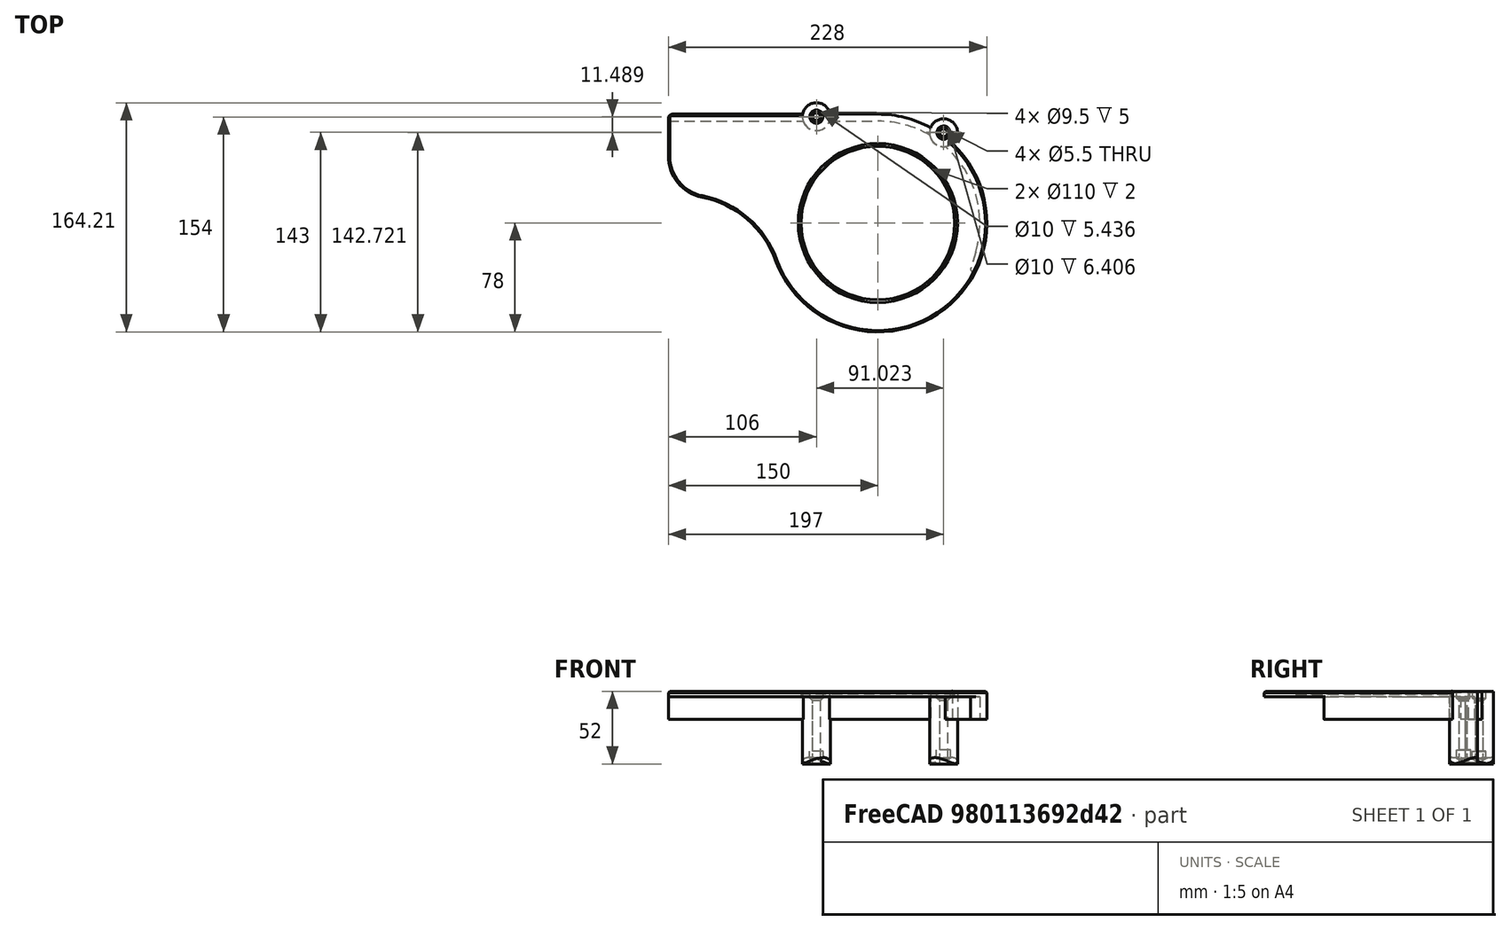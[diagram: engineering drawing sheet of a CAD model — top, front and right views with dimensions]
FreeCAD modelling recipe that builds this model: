
FCSTD DOCUMENT  (FreeCAD 0.19R)
Label: R2
License: All rights reserved
LicenseURL: http://en.wikipedia.org/wiki/All_rights_reserved
objects: Sketcher::SketchObject×5, Part::Cylinder×4, PartDesign::Pocket×3, PartDesign::Chamfer×3, PartDesign::Pad×2, PartDesign::Fillet×2, Part::MultiFuse×2, Part::Cut×2, PartDesign::Body×1, Mesh::Feature×1
note: 34 computed .brp shape members not serialized (recipe doc carries the construction recipe); baked Part::Feature solids carry a one-line shape summary decoded from their .brp

FEATURE [Sketcher::SketchObject] Sketch
  FullyConstrained = true
  MapMode = 5
  Support = -> [XY_Plane]
  sketch-geometry (10):
    g0: LineSegment StartX=0 StartY=0 StartZ=0 EndX=121.094 EndY=169.768 EndZ=0
    g1: LineSegment StartX=-81.2548 StartY=143.617 StartZ=0 EndX=0 EndY=0 EndZ=0
    g2: Circle CenterX=0 CenterY=0 CenterZ=0 NormalX=0 NormalY=0 NormalZ=1 AngleXU=0 Radius=73
    g3: LineSegment StartX=-228.06 StartY=73 StartZ=0 EndX=0 EndY=73 EndZ=0
    g4: LineSegment StartX=2.39e-14 StartY=78 StartZ=0 EndX=-150 EndY=78 EndZ=0
    g5: ArcOfCircle CenterX=0 CenterY=0 CenterZ=0 NormalX=0 NormalY=0 NormalZ=1 AngleXU=0 Radius=78 StartAngle=3.48916 EndAngle=7.85398
    g6: LineSegment StartX=-150 StartY=78 StartZ=0 EndX=-150 EndY=48 EndZ=0
    g7: ArcOfCircle CenterX=-120 CenterY=48 CenterZ=0 NormalX=0 NormalY=0 NormalZ=1 AngleXU=0 Radius=30 StartAngle=3.14159 EndAngle=4.51567
    g8: ArcOfCircle CenterX=-139.648 CenterY=-50.5912 CenterZ=0 NormalX=0 NormalY=0 NormalZ=1 AngleXU=0 Radius=70.53 StartAngle=0.347568 EndAngle=1.37408
    g9: Circle CenterX=0 CenterY=0 CenterZ=0 NormalX=0 NormalY=0 NormalZ=1 AngleXU=0 Radius=55
  constraints (28):
    c: Coincident(g0,g-1)
    c: Coincident(g1,g-1)
    c: Angle(g1) = -1.05592
    c: Angle(g0,g1) = 1.13446
    c: Coincident(g2,g-1)
    c: Radius(g2) = 73
    c: Tangent(g3,g2)
    c: Angle(g3) = 0
    c: PointOnObject(g4,g-2)
    c: Coincident(g5,g-1)
    c: Coincident(g5,g4)
    c: Radius(g5) = 78
    c: Coincident(g6,g4)
    c: Vertical(g6)
    c: Tangent(g5,g8) = 1.5708
    c: Tangent(g8,g7) = 1.5708
    c: Tangent(g7,g6) = -1.5708
    c: Distance(g4) = 150
    c: Radius(g7) = 30
    c: Radius(g8) = 70.53
    c: Horizontal(g4)
    c: Distance(g6) = 30
    c: Distance(g0) = 208.53
    c: Distance(g1) = 165.01
    c: Distance(g3) = 228.06
    c: PointOnObject(g3,g-2)
    c: Coincident(g9,g5)
    c: Radius(g9) = 55
FEATURE [PartDesign::Pad] Pad
  Direction = (1,1,1)
  Length = 20
  Length2 = 100
  Profile = -> Sketch
  Type = 0
FEATURE [Sketcher::SketchObject] Sketch001
  FullyConstrained = true
  MapMode = 5
  Placement = pos=(0,0,0) rot=(1,0,0;3.14159rad)
  Support = -> [Pad]
  sketch-geometry (4):
    g0: LineSegment StartX=-300 StartY=-73 StartZ=0 EndX=0 EndY=-73 EndZ=0
    g1: ArcOfCircle CenterX=0 CenterY=0 CenterZ=0 NormalX=0 NormalY=0 NormalZ=1 AngleXU=0 Radius=73 StartAngle=4.71239 EndAngle=6.57087
    g2: LineSegment StartX=70 StartY=20.7123 StartZ=0 EndX=34.9593 EndY=139.137 EndZ=0
    g3: LineSegment StartX=34.9593 StartY=139.137 StartZ=0 EndX=-300 EndY=-73 EndZ=0
  constraints (11):
    c: PointOnObject(g0,g-2)
    c: Horizontal(g0)
    c: Coincident(g1,g-1)
    c: Coincident(g1,g0)
    c: DistanceX(g1) = 70
    c: Radius(g1) = 73
    c: Tangent(g1,g2) = -1.5708
    c: Coincident(g2,g3)
    c: Coincident(g3,g0)
    c: Distance(g2) = 123.5
    c: Distance(g0) = 300
FEATURE [PartDesign::Pocket] Pocket
  BaseFeature = -> Pad
  Length = 16
  Length2 = 100
  Profile = -> Sketch001
  Type = 0
FEATURE [Sketcher::SketchObject] Sketch002
  FullyConstrained = true
  MapMode = 5
  Placement = pos=(0,0,20) rot=(0,0,1;0rad)
  Support = -> [Pocket]
  sketch-geometry (4):
    g0: LineSegment StartX=-75 StartY=129.904 StartZ=0 EndX=0 EndY=0 EndZ=0
    g1: LineSegment StartX=0 StartY=0 StartZ=0 EndX=88.1678 EndY=121.353 EndZ=0
    g2: Circle CenterX=-44 CenterY=76.2102 CenterZ=0 NormalX=0 NormalY=0 NormalZ=1 AngleXU=0 Radius=10
    g3: Circle CenterX=47.0228 CenterY=64.7214 CenterZ=0 NormalX=0 NormalY=0 NormalZ=1 AngleXU=0 Radius=10
  constraints (12):
    c: Coincident(g0,g-1)
    c: Angle(g0) = -1.0472
    c: Coincident(g1,g-1)
    c: Angle(g1,g0) = 1.15192
    c: Distance(g1) = 150
    c: Distance(g0) = 150
    c: Diameter(g3) = 20
    c: Equal(g3,g2)
    c: PointOnObject(g2,g0)
    c: PointOnObject(g3,g1)
    c: Distance(g-1,g3) = 80
    c: Distance(g-1,g2) = 88
FEATURE [PartDesign::Pad] Pad001
  BaseFeature = -> Pocket
  Direction = (1,1,1)
  Length = 52
  Length2 = 100
  Profile = -> Sketch002
  Reversed = true
  Type = 0
FEATURE [Sketcher::SketchObject] Sketch003
  ExternalGeometry = -> [Pad001]
  FullyConstrained = true
  MapMode = 5
  Placement = pos=(0,0,20) rot=(0,0,1;0rad)
  Support = -> [Pad001]
  sketch-geometry (2):
    g0: Circle CenterX=-44 CenterY=76.2102 CenterZ=0 NormalX=0 NormalY=0 NormalZ=1 AngleXU=0 Radius=2.75
    g1: Circle CenterX=47.0228 CenterY=64.7214 CenterZ=0 NormalX=0 NormalY=0 NormalZ=1 AngleXU=0 Radius=2.75
  constraints (4):
    c: Diameter(g0) = 5.5
    c: Equal(g0,g1)
    c: Coincident(g0,g-3)
    c: Coincident(g1,g-4)
FEATURE [PartDesign::Pocket] Pocket001
  BaseFeature = -> Pad001
  Length = 5
  Length2 = 100
  Profile = -> Sketch003
  Type = 1
FEATURE [Sketcher::SketchObject] Sketch004
  ExternalGeometry = -> [Pocket001]
  FullyConstrained = true
  MapMode = 5
  Placement = pos=(0,0,20) rot=(0,0,1;0rad)
  Support = -> [Pocket001]
  sketch-geometry (2):
    g0: Circle CenterX=47.0228 CenterY=64.7214 CenterZ=0 NormalX=0 NormalY=0 NormalZ=1 AngleXU=0 Radius=4.75
    g1: Circle CenterX=-44 CenterY=76.2102 CenterZ=0 NormalX=0 NormalY=0 NormalZ=1 AngleXU=0 Radius=4.75
  constraints (4):
    c: Diameter(g1) = 9.5
    c: Coincident(g1,g-4)
    c: Coincident(g0,g-5)
    c: Diameter(g0) = 9.5
FEATURE [PartDesign::Pocket] Pocket002
  BaseFeature = -> Pocket001
  Length = 5
  Length2 = 100
  Profile = -> Sketch004
  Type = 0
FEATURE [Part::Cylinder] Cylinder
  Angle = 360
  AttacherType = Attacher::AttachEngine3D
  Height = 100
  Placement = pos=(0,0,-42) rot=(-0.810679,0.585491,0;1.5708rad)
  Radius = 14.5
FEATURE [Part::Cylinder] Cylinder001
  Angle = 360
  AttacherType = Attacher::AttachEngine3D
  Height = 100
  Placement = pos=(0,0,-42) rot=(-0.864712,-0.502269,0;1.5708rad)
  Radius = 14.5
FEATURE [Part::Cylinder] Cylinder002
  Angle = 360
  AttacherType = Attacher::AttachEngine3D
  Height = 10
  Placement = pos=(-44,76,-33) rot=(0,0,1;0rad)
  Radius = 5
FEATURE [Part::Cylinder] Cylinder003
  Angle = 360
  AttacherType = Attacher::AttachEngine3D
  Height = 10
  Placement = pos=(47,65,-32) rot=(0,0,1;0rad)
  Radius = 5
FEATURE [PartDesign::Fillet] Fillet
  Base = -> Pocket002 [Edge62]
  BaseFeature = -> Pocket002
  Radius = 2
  SupportTransform = false
FEATURE [PartDesign::Fillet] Fillet001
  Base = -> Fillet [Edge54]
  BaseFeature = -> Fillet
  Radius = 3
  SupportTransform = false
FEATURE [PartDesign::Chamfer] Chamfer
  Angle = 45
  Base = -> Fillet001 [Edge24]
  BaseFeature = -> Fillet001
  ChamferType = 0
  FlipDirection = false
  Size = 2
  Size2 = 1
  SupportTransform = false
FEATURE [PartDesign::Chamfer] Chamfer001
  Angle = 45
  Base = -> Chamfer [Edge8]
  BaseFeature = -> Chamfer
  ChamferType = 0
  FlipDirection = false
  Size = 1
  Size2 = 1
  SupportTransform = false
FEATURE [PartDesign::Chamfer] Chamfer002
  Angle = 45
  Base = -> Chamfer001 [Edge103,Edge109]
  BaseFeature = -> Chamfer001
  ChamferType = 0
  FlipDirection = false
  Size = 1.6
  Size2 = 1
  SupportTransform = false
FEATURE [PartDesign::Body] Body
  Group = -> [Sketch,Pad,Sketch001,Pocket,Sketch002,Pad001,Sketch003,Pocket001,Sketch004,Pocket002,Fillet,Fillet001,Chamfer,Chamfer001,Chamfer002]
  Origin = -> Origin
  Tip = -> Chamfer002
FEATURE [Part::MultiFuse] Fusion
  Shapes = -> [Cylinder,Cylinder001]
FEATURE [Part::Cut] Cut
  Base = -> Chamfer002
  Tool = -> Fusion
FEATURE [Part::MultiFuse] Fusion001
  Shapes = -> [Cylinder003,Cylinder002]
FEATURE [Part::Cut] Cut001
  Base = -> Cut
  Tool = -> Fusion001
FEATURE [Mesh::Feature] Mesh  label="Cut001 (Meshed)"
